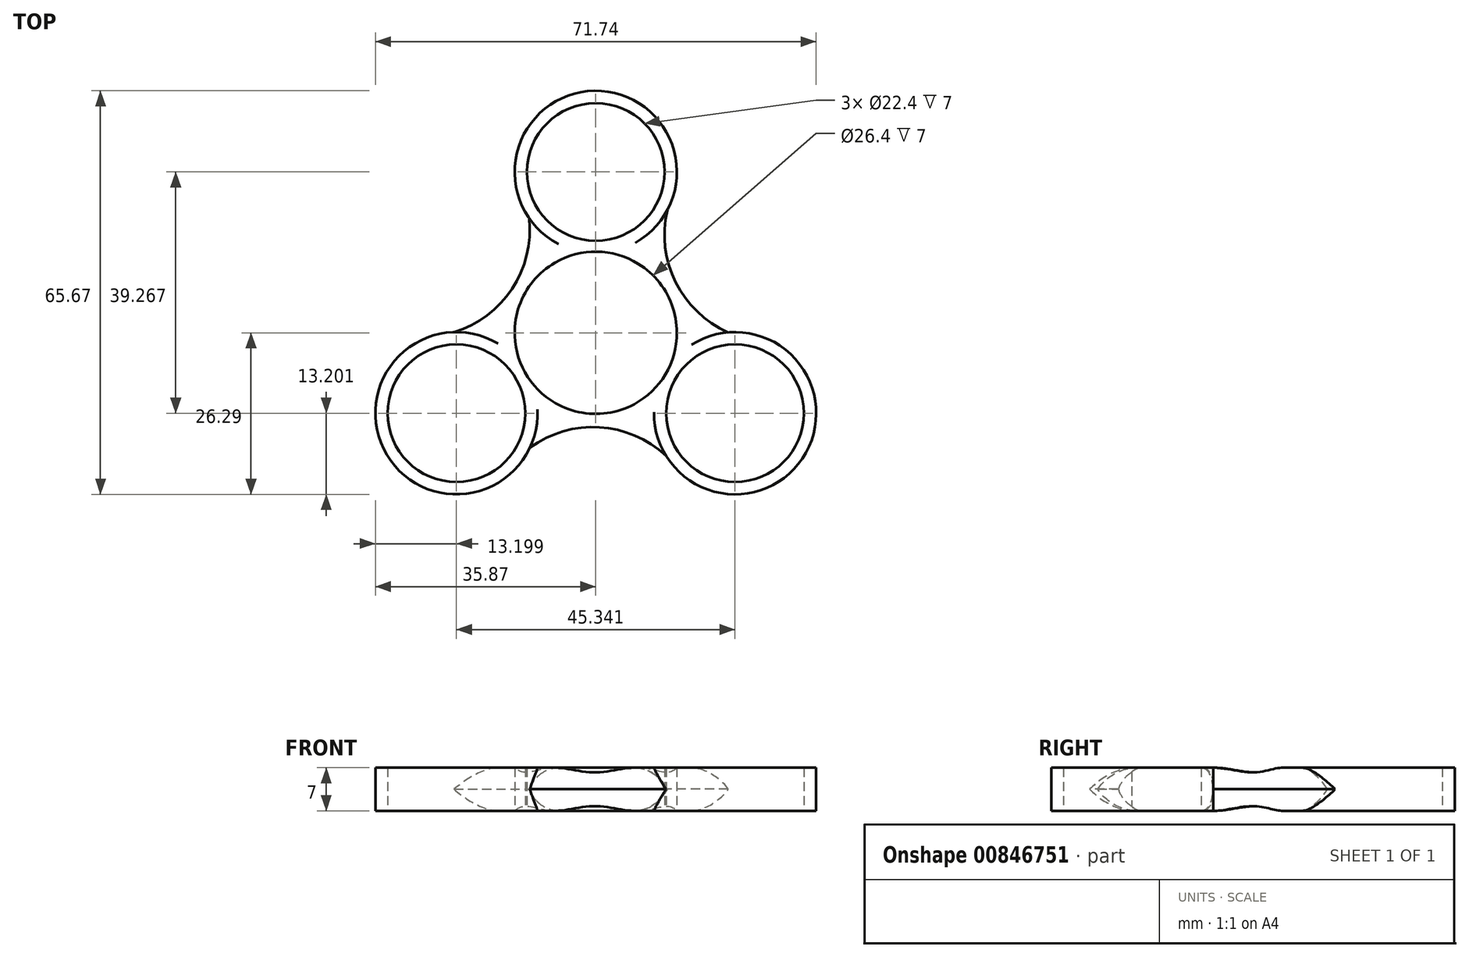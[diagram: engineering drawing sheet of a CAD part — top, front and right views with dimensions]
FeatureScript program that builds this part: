
annotation { "Feature Type Name" : "Feature", "Feature Type Description" : "" }
export const myFeature = defineFeature(function(context is Context, id is Id, definition is map)
    precondition{}
    {
        {
            var Q0;
            Q0=qCreatedBy(makeId("Top.planeOp"),FACE);
            var sketch = newSketch(context, id + "F0", { "sketchPlane" : qUnion([Q0])});
            skCircle(sketch, "E0", {"center": v(0, 0) * mm, "radius": 11.2 * mm});
            skCircle(sketch, "E1", {"center": v(0, 0) * mm, "radius": 13.2 * mm});
            skCircle(sketch, "E2", {"center": v(0, 26.18) * mm, "radius": 11.2 * mm});
            skCircle(sketch, "E3", {"center": v(0, 26.18) * mm, "radius": 13.2 * mm});
            skCircle(sketch, "E4.1.0", {"center": v(-22.67, -13.09) * mm, "radius": 11.2 * mm});
            skCircle(sketch, "E4.1.1", {"center": v(-22.67, -13.09) * mm, "radius": 13.2 * mm});
            skCircle(sketch, "E4.2.0", {"center": v(22.67, -13.09) * mm, "radius": 11.2 * mm});
            skCircle(sketch, "E4.2.1", {"center": v(22.67, -13.09) * mm, "radius": 13.2 * mm});
            skArc(sketch, "E5", {"start": v(-24.38, 0) * mm, "mid": v(-12.46, 9.76) * mm, "end": v(-13.16, 25.16) * mm});
            skArc(sketch, "E6.1.0", {"start": v(12.19, -21.11) * mm, "mid": v(-2.23, -15.67) * mm, "end": v(-15.2, -23.98) * mm});
            skArc(sketch, "E6.2.0", {"start": v(12.19, 21.11) * mm, "mid": v(14.68, 5.9) * mm, "end": v(28.37, -1.18) * mm});
            skSolve(sketch);
        }
        {
            var Q0;
            Q0 = qSketchRegion(id + "F0", true);
            extrude(context, id + "F1", {"entities" : qUnion([Q0]), "depth" : 7 * mm, "offsetDistance" : 25 * mm});
        }
        {
            var Q0;
            Q0=makeQuery(id+"F1.opExtrude","CAP_EDGE",EDGE,{"disambiguationData":[OSD([sQuery(id+"F0.wireOp",EDGE,"E5")])],"isStart":false});
            var Q1;
            Q1=makeQuery(id+"F1.opExtrude","CAP_EDGE",EDGE,{"disambiguationData":[OSD([sQuery(id+"F0.wireOp",EDGE,"E5")])],"isStart":true});
            var Q2;
            Q2=makeQuery(id+"F1.opExtrude","CAP_EDGE",EDGE,{"disambiguationData":[OSD([sQuery(id+"F0.wireOp",EDGE,"E6.1.0")])],"isStart":true});
            var Q3;
            Q3=makeQuery(id+"F1.opExtrude","CAP_EDGE",EDGE,{"disambiguationData":[OSD([sQuery(id+"F0.wireOp",EDGE,"E6.2.0")])],"isStart":true});
            var Q4;
            Q4=makeQuery(id+"F1.opExtrude","CAP_EDGE",EDGE,{"disambiguationData":[OSD([sQuery(id+"F0.wireOp",EDGE,"E6.2.0")])],"isStart":false});
            var Q5;
            Q5=makeQuery(id+"F1.opExtrude","CAP_EDGE",EDGE,{"disambiguationData":[OSD([sQuery(id+"F0.wireOp",EDGE,"E6.1.0")])],"isStart":false});
            fillet(context, id + "F2", {"entities" : qUnion([Q0, Q1, Q2, Q3, Q4, Q5]), "radius" : 5 * mm, "tangentPropagation" : true, "allowEdgeOverflow" : false});
        }
    });
